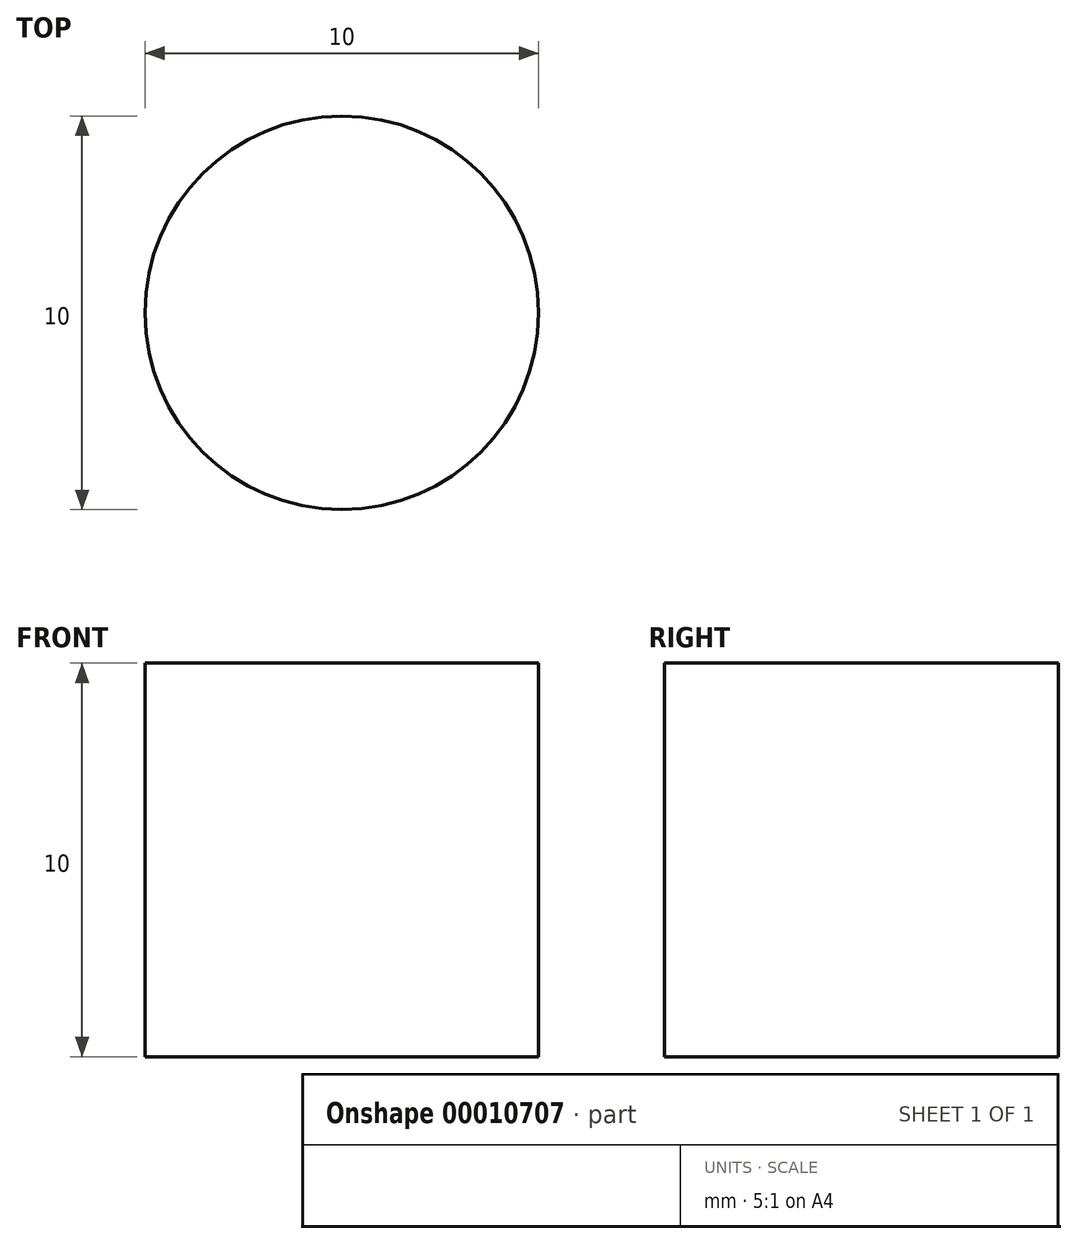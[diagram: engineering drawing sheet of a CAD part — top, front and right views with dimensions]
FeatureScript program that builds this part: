
annotation { "Feature Type Name" : "Feature", "Feature Type Description" : "" }
export const myFeature = defineFeature(function(context is Context, id is Id, definition is map)
    precondition{}
    {
        {
            var Q0;
            Q0=qCreatedBy(makeId("Top.planeOp"),FACE);
            var sketch = newSketch(context, id + "F0", { "sketchPlane" : qUnion([Q0])});
            skCircle(sketch, "E0", {"center": v(0, 0) * mm, "radius": 5 * mm});
            skCircle(sketch, "E1", {"center": v(0, 0) * mm, "radius": 5.55 * mm});
            skSolve(sketch);
        }
        {
            var Q0;
            Q0=makeQuery(id+"F0.imprint","IMPRINT",FACE,{"disambiguationData":[TD([[makeQuery(id+"F0.imprint","IMPRINT",EDGE,{"derivedFrom":sQuery(id+"F0.wireOp",EDGE,"E0")}),1.0]])]});
            extrude(context, id + "F1", {"entities" : qUnion([Q0]), "depth" : 10 * mm});
        }
    });
